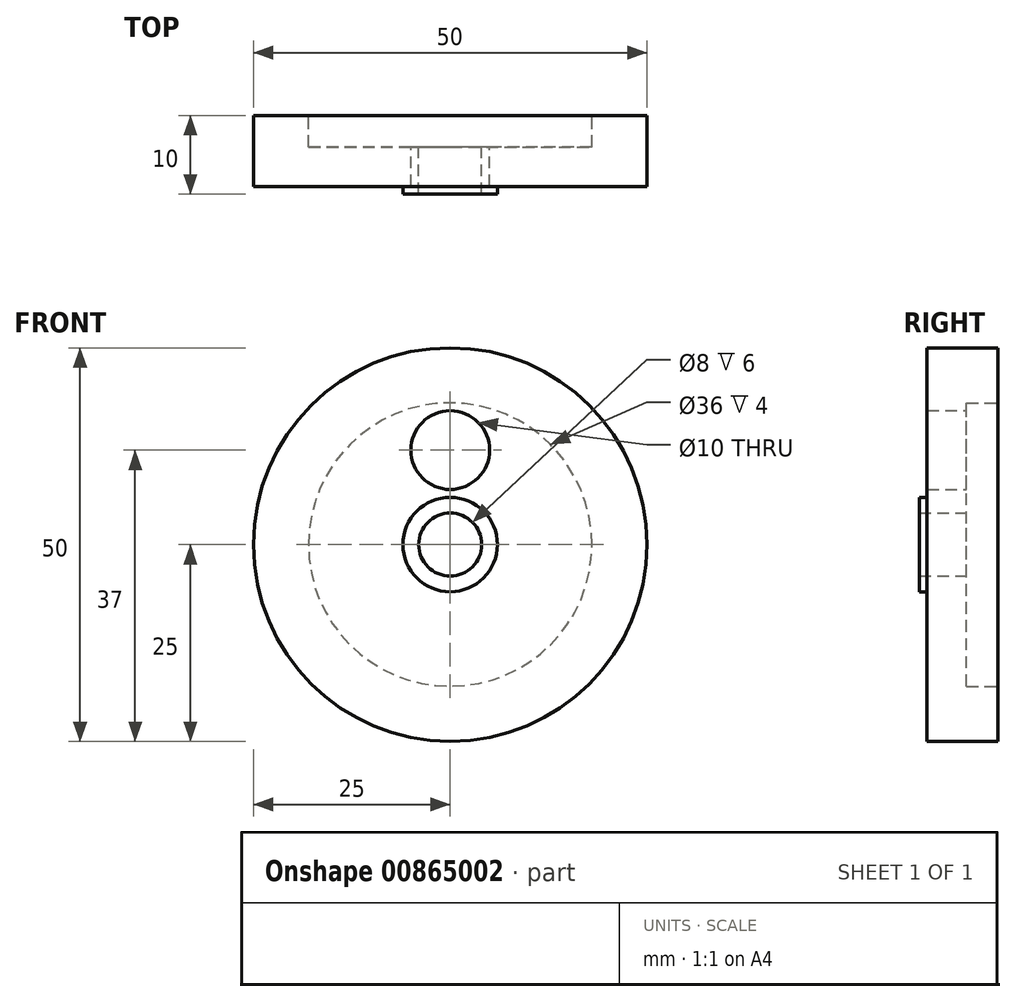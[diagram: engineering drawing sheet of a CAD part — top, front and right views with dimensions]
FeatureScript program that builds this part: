
annotation { "Feature Type Name" : "Feature", "Feature Type Description" : "" }
export const myFeature = defineFeature(function(context is Context, id is Id, definition is map)
    precondition{}
    {
        {
            var Q0;
            Q0=qCreatedBy(makeId("Front.planeOp"),FACE);
            var sketch = newSketch(context, id + "F0", { "sketchPlane" : qUnion([Q0])});
            skCircle(sketch, "E0", {"center": v(0, 0) * mm, "radius": 4 * mm});
            skCircle(sketch, "E1", {"center": v(0, 0) * mm, "radius": 6 * mm});
            skCircle(sketch, "E2", {"center": v(0, 0) * mm, "radius": 18 * mm});
            skCircle(sketch, "E3", {"center": v(0, 0) * mm, "radius": 25 * mm});
            skCircle(sketch, "E4", {"center": v(0, 0) * mm, "radius": 12 * mm, "construction": true});
            skCircle(sketch, "E5", {"center": v(0, 12) * mm, "radius": 5 * mm});
            skSolve(sketch);
        }
        {
            var Q0;
            Q0=makeQuery(id+"F0.imprint","IMPRINT",FACE,{"disambiguationData":[TD([[makeQuery(id+"F0.imprint","IMPRINT",EDGE,{"derivedFrom":sQuery(id+"F0.wireOp",EDGE,"E2")}),-1.0]])]});
            var Q1;
            Q1=makeQuery(id+"F0.imprint","IMPRINT",FACE,{"disambiguationData":[TD([[makeQuery(id+"F0.imprint","IMPRINT",EDGE,{"derivedFrom":sQuery(id+"F0.wireOp",EDGE,"E1")}),-1.0]])]});
            var Q2;
            Q2=makeQuery(id+"F0.imprint","IMPRINT",FACE,{"disambiguationData":[TD([[makeQuery(id+"F0.imprint","IMPRINT",EDGE,{"derivedFrom":sQuery(id+"F0.wireOp",EDGE,"E0")}),-1.0]])]});
            var Q3;
            Q3=makeQuery(id+"F0.imprint","IMPRINT",FACE,{"disambiguationData":[TD([[makeQuery(id+"F0.imprint","IMPRINT",EDGE,{"derivedFrom":sQuery(id+"F0.wireOp",EDGE,"E5")}),1.0]])]});
            extrude(context, id + "F1", {"entities" : qUnion([Q0, Q1, Q2, Q3]), "depth" : 9 * mm, "offsetDistance" : 25 * mm});
        }
        {
            var Q0;
            Q0=makeQuery(id+"F0.imprint","IMPRINT",FACE,{"disambiguationData":[TD([[makeQuery(id+"F0.imprint","IMPRINT",EDGE,{"derivedFrom":sQuery(id+"F0.wireOp",EDGE,"E0")}),-1.0]])]});
            extrude(context, id + "F2", {"entities" : qUnion([Q0]), "operationType" : NewBodyOperationType.ADD, "depth" : 10 * mm, "offsetDistance" : 25 * mm});
        }
        {
            var Q0;
            Q0=makeQuery(id+"F0.imprint","IMPRINT",FACE,{"disambiguationData":[TD([[makeQuery(id+"F0.imprint","IMPRINT",EDGE,{"derivedFrom":sQuery(id+"F0.wireOp",EDGE,"E1")}),-1.0]])]});
            var Q1;
            Q1=makeQuery(id+"F0.imprint","IMPRINT",FACE,{"disambiguationData":[TD([[makeQuery(id+"F0.imprint","IMPRINT",EDGE,{"derivedFrom":sQuery(id+"F0.wireOp",EDGE,"E0")}),-1.0]])]});
            var Q2;
            Q2=makeQuery(id+"F0.imprint","IMPRINT",FACE,{"disambiguationData":[TD([[makeQuery(id+"F0.imprint","IMPRINT",EDGE,{"derivedFrom":sQuery(id+"F0.wireOp",EDGE,"E5")}),1.0]])]});
            extrude(context, id + "F3", {"entities" : qUnion([Q0, Q1, Q2]), "operationType" : NewBodyOperationType.REMOVE, "depth" : 4 * mm, "offsetDistance" : 25 * mm});
        }
        {
            var Q0;
            Q0=makeQuery(id+"F0.imprint","IMPRINT",FACE,{"disambiguationData":[TD([[makeQuery(id+"F0.imprint","IMPRINT",EDGE,{"derivedFrom":sQuery(id+"F0.wireOp",EDGE,"E5")}),1.0]])]});
            extrude(context, id + "F4", {"entities" : qUnion([Q0]), "operationType" : NewBodyOperationType.REMOVE, "endBound" : BoundingType.THROUGH_ALL, "depth" : 25 * mm, "offsetDistance" : 25 * mm});
        }
    });
